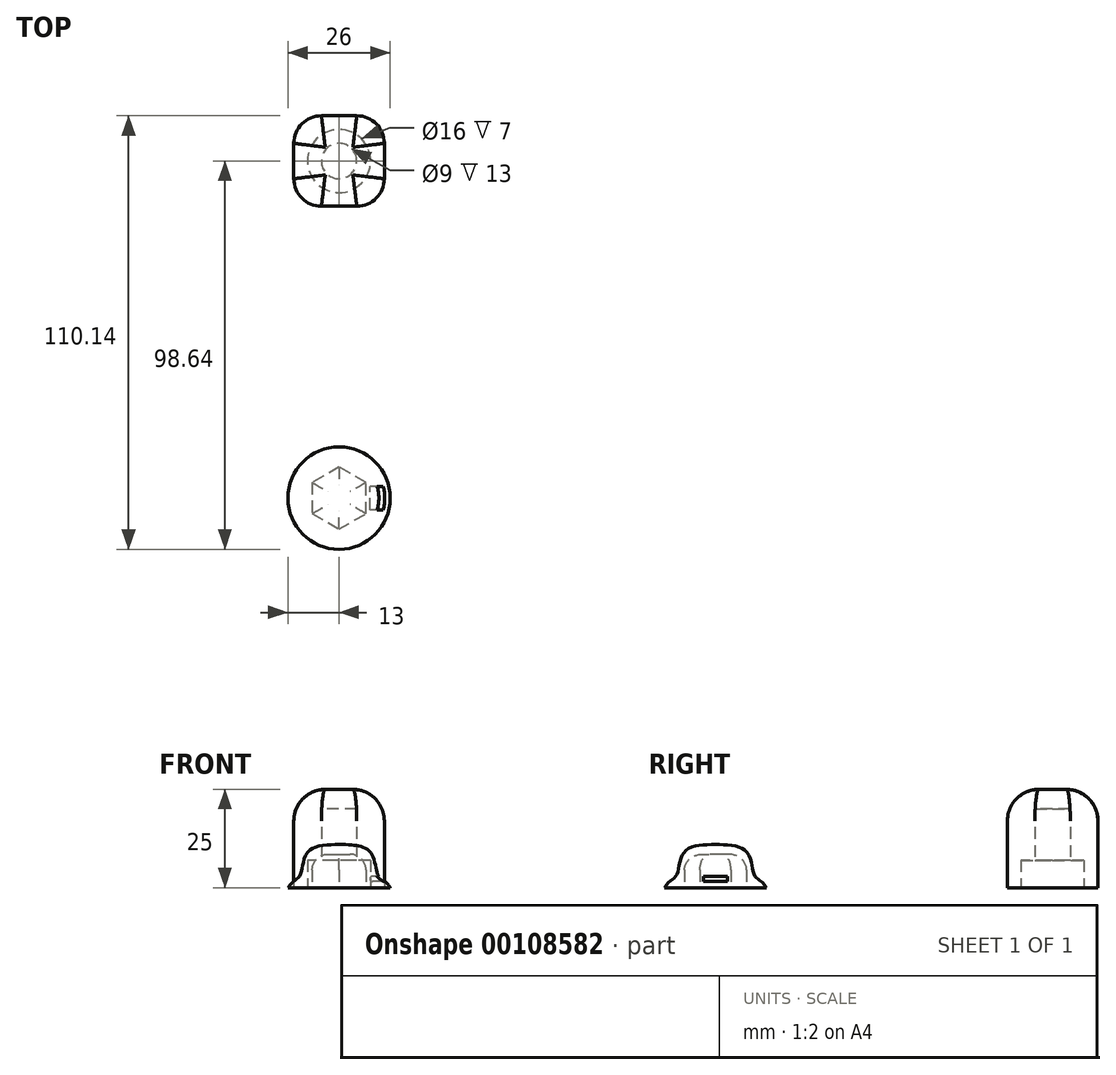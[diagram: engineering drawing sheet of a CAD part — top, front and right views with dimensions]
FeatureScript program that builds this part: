
annotation { "Feature Type Name" : "Feature", "Feature Type Description" : "" }
export const myFeature = defineFeature(function(context is Context, id is Id, definition is map)
    precondition{}
    {
        {
            var Q0;
            Q0=qCreatedBy(makeId("Top.planeOp"),FACE);
            var sketch = newSketch(context, id + "F0", { "sketchPlane" : qUnion([Q0])});
            skLineSegment(sketch, "E0.bottom", {"start": v(-15, 48.04) * mm, "end": v(15, 48.04) * mm, "construction": true});
            skLineSegment(sketch, "E0.top", {"start": v(-15, -48.04) * mm, "end": v(15, -48.04) * mm, "construction": true});
            skLineSegment(sketch, "E0.left", {"start": v(-15, 48.04) * mm, "end": v(-15, -48.04) * mm, "construction": true});
            skLineSegment(sketch, "E0.right", {"start": v(15, 48.04) * mm, "end": v(15, -48.04) * mm, "construction": true});
            skCircle(sketch, "E1", {"center": v(0, 0) * mm, "radius": 8 * mm});
            skCircle(sketch, "E2", {"center": v(0, 0) * mm, "radius": 4.5 * mm});
            skLineSegment(sketch, "E3.bottom", {"start": v(-11.5, 11.5) * mm, "end": v(11.5, 11.5) * mm});
            skLineSegment(sketch, "E3.top", {"start": v(-11.5, -11.5) * mm, "end": v(11.5, -11.5) * mm});
            skLineSegment(sketch, "E3.left", {"start": v(-11.5, 11.5) * mm, "end": v(-11.5, -11.5) * mm});
            skLineSegment(sketch, "E3.right", {"start": v(11.5, 11.5) * mm, "end": v(11.5, -11.5) * mm});
            skLineSegment(sketch, "E4.bottom", {"start": v(-4, 4) * mm, "end": v(4, 4) * mm, "construction": true});
            skLineSegment(sketch, "E4.top", {"start": v(-4, -10) * mm, "end": v(4, -10) * mm, "construction": true});
            skLineSegment(sketch, "E4.left", {"start": v(-4, 4) * mm, "end": v(-4, -10) * mm, "construction": true});
            skLineSegment(sketch, "E4.right", {"start": v(4, 4) * mm, "end": v(4, -10) * mm, "construction": true});
            skSolve(sketch);
        }
        {
            var Q0;
            Q0 = qSketchRegion(id + "F0", true);
            var Q1;
            Q1=makeQuery(id+"F0.imprint","IMPRINT",FACE,{"disambiguationData":[TD([[makeQuery(id+"F0.imprint","IMPRINT",EDGE,{"derivedFrom":sQuery(id+"F0.wireOp",EDGE,"E1")}),1.0]])]});
            var Q2;
            Q2=makeQuery(id+"F0.imprint","IMPRINT",FACE,{"disambiguationData":[TD([[makeQuery(id+"F0.imprint","IMPRINT",EDGE,{"derivedFrom":sQuery(id+"F0.wireOp",EDGE,"E2")}),1.0]])]});
            extrude(context, id + "F1", {"entities" : qUnion([Q0, Q1, Q2]), "depth" : 25 * mm});
        }
        {
            var Q0;
            Q0=makeQuery(id+"F1.opExtrude","CAP_EDGE",EDGE,{"disambiguationData":[OSD([sQuery(id+"F0.wireOp",EDGE,"E3.top")])],"isStart":false});
            var Q1;
            Q1=makeQuery(id+"F1.opExtrude","CAP_EDGE",EDGE,{"disambiguationData":[OSD([sQuery(id+"F0.wireOp",EDGE,"E3.left")])],"isStart":false});
            var Q2;
            Q2=makeQuery(id+"F1.opExtrude","CAP_EDGE",EDGE,{"disambiguationData":[OSD([sQuery(id+"F0.wireOp",EDGE,"E3.bottom")])],"isStart":false});
            var Q3;
            Q3=makeQuery(id+"F1.opExtrude","CAP_EDGE",EDGE,{"disambiguationData":[OSD([sQuery(id+"F0.wireOp",EDGE,"E3.right")])],"isStart":false});
            fillet(context, id + "F2", {"entities" : qUnion([Q0, Q1, Q2, Q3]), "radius" : 8 * mm, "tangentPropagation" : true, "allowEdgeOverflow" : false});
        }
        {
            var Q0;
            Q0=makeQuery(id+"F1.opExtrude","SWEPT_EDGE",EDGE,{"disambiguationData":[OSD([sQuery(id+"F0.wireOp",EDGE,"E3.top"),sQuery(id+"F0.wireOp",EDGE,"E3.left")])]});
            var Q1;
            Q1=makeQuery(id+"F1.opExtrude","SWEPT_EDGE",EDGE,{"disambiguationData":[OSD([sQuery(id+"F0.wireOp",EDGE,"E3.top"),sQuery(id+"F0.wireOp",EDGE,"E3.right")])]});
            var Q2;
            Q2=makeQuery(id+"F1.opExtrude","SWEPT_EDGE",EDGE,{"disambiguationData":[OSD([sQuery(id+"F0.wireOp",EDGE,"E3.bottom"),sQuery(id+"F0.wireOp",EDGE,"E3.right")])]});
            var Q3;
            Q3=makeQuery(id+"F1.opExtrude","SWEPT_EDGE",EDGE,{"disambiguationData":[OSD([sQuery(id+"F0.wireOp",EDGE,"E3.bottom"),sQuery(id+"F0.wireOp",EDGE,"E3.left")])]});
            fillet(context, id + "F3", {"entities" : qUnion([Q0, Q1, Q2, Q3]), "radius" : 7 * mm, "tangentPropagation" : true, "allowEdgeOverflow" : false});
        }
        {
            var Q0;
            Q0=makeQuery(id+"F0.imprint","IMPRINT",FACE,{"disambiguationData":[TD([[makeQuery(id+"F0.imprint","IMPRINT",EDGE,{"derivedFrom":sQuery(id+"F0.wireOp",EDGE,"E2")}),1.0]])]});
            extrude(context, id + "F4", {"entities" : qUnion([Q0]), "operationType" : NewBodyOperationType.REMOVE, "depth" : 20 * mm});
        }
        {
            var Q0;
            Q0=makeQuery(id+"F0.imprint","IMPRINT",FACE,{"disambiguationData":[TD([[makeQuery(id+"F0.imprint","IMPRINT",EDGE,{"derivedFrom":sQuery(id+"F0.wireOp",EDGE,"E1")}),1.0]])]});
            extrude(context, id + "F5", {"entities" : qUnion([Q0]), "operationType" : NewBodyOperationType.REMOVE, "depth" : 7 * mm});
        }
        {
            var Q0;
            Q0=qCreatedBy(makeId("Right.planeOp"),FACE);
            var sketch = newSketch(context, id + "F6", { "sketchPlane" : qUnion([Q0])});
            skLineSegment(sketch, "E5.bottom", {"start": v(-93.64, 0) * mm, "end": v(-77.64, 0) * mm, "construction": true});
            skLineSegment(sketch, "E5.top", {"start": v(-93.64, 9) * mm, "end": v(-77.64, 9) * mm, "construction": true});
            skLineSegment(sketch, "E5.left", {"start": v(-93.64, 0) * mm, "end": v(-93.64, 9) * mm, "construction": true});
            skLineSegment(sketch, "E5.right", {"start": v(-77.64, 0) * mm, "end": v(-77.64, 9) * mm, "construction": true});
            skLineSegment(sketch, "E6", {"start": v(-85.64, 9) * mm, "end": v(-85.64, 0) * mm});
            skLineSegment(sketch, "E7", {"start": v(-85.64, 0) * mm, "end": v(-72.64, 0) * mm, "construction": true});
            skLineSegment(sketch, "E8.MirrorCS", {"start": v(-85.64, 0) * mm, "end": v(-98.64, 0) * mm});
            skLineSegment(sketch, "E9", {"start": v(-85.64, 9) * mm, "end": v(-85.64, 11) * mm});
            skFitSpline(sketch, "E10", {"points": [v(-72.64, 0) * mm, v(-77.64, 9) * mm, v(-85.64, 11) * mm, v(-93.64, 9) * mm, v(-95.64, 3) * mm, v(-98.64, 0) * mm], "startDerivative": vector(-13.58, 24.81) * mm, "endDerivative": vector(-21.16, -38.65) * mm});
            skFitSpline(sketch, "E11", {"points": [v(-72.64, 0) * mm, v(-77.64, 9) * mm, v(-85.64, 11) * mm, v(-93.64, 9) * mm, v(-95.64, 3) * mm, v(-98.64, 0) * mm], "startDerivative": vector(-13.58, 24.81) * mm, "endDerivative": vector(-21.16, -38.65) * mm});
            skSolve(sketch);
        }
        {
            var Q0;
            Q0=makeQuery(id+"F6.imprint","IMPRINT",FACE,{"disambiguationData":[TD([[makeQuery(id+"F6.imprint","IMPRINT",EDGE,{"derivedFrom":sQuery(id+"F6.wireOp",EDGE,"E6")}),-1.0]])]});
            var Q1;
            Q1=sQuery(id+"F6.wireOp",EDGE,"E6");
            revolve(context, id + "F7", {"entities" : qUnion([Q0]), "axis" : qUnion([Q1]), "revolveType" : RevolveType.FULL});
        }
        {
            var Q0;
            Q0=makeQuery(id+"F7.opRevolve","SWEPT_FACE",FACE,{"disambiguationData":[OSD([sQuery(id+"F6.wireOp",EDGE,"E8.MirrorCS")])]});
            var sketch = newSketch(context, id + "F8", { "sketchPlane" : qUnion([Q0])});
            skCircle(sketch, "E12.0", {"center": v(0, 85.64) * mm, "radius": 13 * mm, "construction": true});
            skCircle(sketch, "E13.cCircle", {"center": v(0, 85.64) * mm, "radius": 7.9 * mm, "construction": true});
            skLineSegment(sketch, "E13.0", {"start": v(-6.84, 89.6) * mm, "end": v(0, 93.54) * mm});
            skLineSegment(sketch, "E13.1", {"start": v(0, 93.54) * mm, "end": v(6.84, 89.6) * mm});
            skLineSegment(sketch, "E13.2", {"start": v(6.84, 89.6) * mm, "end": v(6.84, 81.7) * mm});
            skLineSegment(sketch, "E13.3", {"start": v(6.84, 81.7) * mm, "end": v(0, 77.74) * mm});
            skLineSegment(sketch, "E13.4", {"start": v(0, 77.74) * mm, "end": v(-6.84, 81.7) * mm});
            skLineSegment(sketch, "E13.5", {"start": v(-6.84, 81.7) * mm, "end": v(-6.84, 89.6) * mm});
            skSolve(sketch);
        }
        {
            var Q0;
            Q0=makeQuery(id+"F8.imprint","IMPRINT",FACE,{"disambiguationData":[TD([[makeQuery(id+"F8.imprint","IMPRINT",EDGE,{"derivedFrom":sQuery(id+"F8.wireOp",EDGE,"E13.0")}),-1.0]])]});
            extrude(context, id + "F9", {"entities" : qUnion([Q0]), "operationType" : NewBodyOperationType.REMOVE, "oppositeDirection" : true, "depth" : 8.5 * mm});
        }
        {
            var Q0;
            Q0=makeQuery(id+"F9.boolean.opBoolean","COPY",EDGE,{"derivedFrom":makeQuery(id+"F9.opExtrude","CAP_EDGE",EDGE,{"disambiguationData":[OSD([sQuery(id+"F8.wireOp",EDGE,"E13.5")])],"isStart":false})});
            var Q1;
            Q1=makeQuery(id+"F9.boolean.opBoolean","COPY",EDGE,{"derivedFrom":makeQuery(id+"F9.opExtrude","CAP_EDGE",EDGE,{"disambiguationData":[OSD([sQuery(id+"F8.wireOp",EDGE,"E13.4")])],"isStart":false})});
            var Q2;
            Q2=makeQuery(id+"F9.boolean.opBoolean","COPY",EDGE,{"derivedFrom":makeQuery(id+"F9.opExtrude","CAP_EDGE",EDGE,{"disambiguationData":[OSD([sQuery(id+"F8.wireOp",EDGE,"E13.3")])],"isStart":false})});
            var Q3;
            Q3=makeQuery(id+"F9.boolean.opBoolean","COPY",EDGE,{"derivedFrom":makeQuery(id+"F9.opExtrude","CAP_EDGE",EDGE,{"disambiguationData":[OSD([sQuery(id+"F8.wireOp",EDGE,"E13.2")])],"isStart":false})});
            var Q4;
            Q4=makeQuery(id+"F9.boolean.opBoolean","COPY",EDGE,{"derivedFrom":makeQuery(id+"F9.opExtrude","CAP_EDGE",EDGE,{"disambiguationData":[OSD([sQuery(id+"F8.wireOp",EDGE,"E13.1")])],"isStart":false})});
            var Q5;
            Q5=makeQuery(id+"F9.boolean.opBoolean","COPY",EDGE,{"derivedFrom":makeQuery(id+"F9.opExtrude","CAP_EDGE",EDGE,{"disambiguationData":[OSD([sQuery(id+"F8.wireOp",EDGE,"E13.0")])],"isStart":false})});
            fillet(context, id + "F10", {"entities" : qUnion([Q0, Q1, Q2, Q3, Q4, Q5]), "radius" : 4 * mm, "tangentPropagation" : true, "allowEdgeOverflow" : false});
        }
        {
            var Q0;
            Q0=makeQuery(id+"F9.boolean.opBoolean","COPY",FACE,{"derivedFrom":makeQuery(id+"F9.opExtrude","SWEPT_FACE",FACE,{"disambiguationData":[OSD([sQuery(id+"F8.wireOp",EDGE,"E13.2")])]})});
            var sketch = newSketch(context, id + "F11", { "sketchPlane" : qUnion([Q0])});
            skLineSegment(sketch, "E14.0", {"start": v(81.7, 4.5) * mm, "end": v(89.6, 4.5) * mm, "construction": true});
            skLineSegment(sketch, "E14.1", {"start": v(89.6, 4.5) * mm, "end": v(89.6, 0) * mm, "construction": true});
            skLineSegment(sketch, "E14.2", {"start": v(81.7, 4.5) * mm, "end": v(81.7, 0) * mm, "construction": true});
            skLineSegment(sketch, "E15", {"start": v(89.6, 2.25) * mm, "end": v(85.64, 2.25) * mm, "construction": true});
            skLineSegment(sketch, "E16", {"start": v(85.64, 2.25) * mm, "end": v(85.64, 4.5) * mm, "construction": true});
            skLineSegment(sketch, "E17", {"start": v(85.64, 2.25) * mm, "end": v(81.7, 2.25) * mm, "construction": true});
            skLineSegment(sketch, "E18.bottom", {"start": v(88.64, 1.65) * mm, "end": v(82.64, 1.65) * mm});
            skLineSegment(sketch, "E18.top", {"start": v(88.64, 2.85) * mm, "end": v(82.64, 2.85) * mm});
            skLineSegment(sketch, "E18.left", {"start": v(88.64, 1.65) * mm, "end": v(88.64, 2.85) * mm});
            skLineSegment(sketch, "E18.right", {"start": v(82.64, 1.65) * mm, "end": v(82.64, 2.85) * mm});
            skSolve(sketch);
        }
        {
            var Q0;
            Q0=makeQuery(id+"F11.imprint","IMPRINT",FACE,{"disambiguationData":[TD([[makeQuery(id+"F11.imprint","IMPRINT",EDGE,{"derivedFrom":sQuery(id+"F11.wireOp",EDGE,"E18.bottom")}),-1.0]])]});
            extrude(context, id + "F12", {"entities" : qUnion([Q0]), "operationType" : NewBodyOperationType.REMOVE, "endBound" : BoundingType.THROUGH_ALL, "oppositeDirection" : true, "depth" : 25 * mm, "hasSecondDirection" : true, "secondDirectionOppositeDirection" : true, "secondDirectionDepth" : 1 * mm});
        }
        {
            var Q0;
            Q0=makeQuery(id+"F12.boolean.opBoolean","COPY",EDGE,{"derivedFrom":makeQuery(id+"F12.opExtrude","CAP_EDGE",EDGE,{"disambiguationData":[OSD([sQuery(id+"F11.wireOp",EDGE,"E18.bottom")])],"isStart":true})});
            var Q1;
            Q1=makeQuery(id+"F12.boolean.opBoolean","COPY",EDGE,{"derivedFrom":makeQuery(id+"F12.opExtrude","CAP_EDGE",EDGE,{"disambiguationData":[OSD([sQuery(id+"F11.wireOp",EDGE,"E18.top")])],"isStart":true})});
            fillet(context, id + "F13", {"entities" : qUnion([Q0, Q1]), "radius" : 0.6 * mm, "tangentPropagation" : true, "allowEdgeOverflow" : false});
        }
    });
